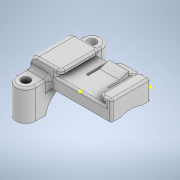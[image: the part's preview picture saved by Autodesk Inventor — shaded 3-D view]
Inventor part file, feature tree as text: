
AUTODESK INVENTOR PART (.ipt)
format: ipt  version: 2020 (Build 240168000, 168)  size: 480,256 bytes
history: native  units: mm
features: fillet x15, sketch x10, extrude x8, projected_geometry x1
ambient origin geometry x8: Origin, YZ Plane, XZ Plane, XY Plane, X Axis, Y Axis, Z Axis, Center Point
bodies: Volumenkörper1 (feature_tree)
feature tree (34):
  extrude  "Extrusion1"  Depth=24.0mm
  extrude  "Extrusion2"  Depth=2.0mm
  extrude  "Extrusion3"  Depth=2.0mm
  fillet  "Rundung1"  Radius=20.0mm
  fillet  "Rundung3"  Radius=44.0mm
  fillet  "Rundung4"  Radius=15.8mm
  fillet  "Rundung5"  Radius=22.2mm
  fillet  "Rundung6"  Radius=18.0mm
  extrude  "Extrusion4"  Depth=15.8mm
  extrude  "Extrusion5"  Depth=10.0mm
  sketch  "Skizze6"  dims[d19=4.5mm d20=5.0mm d21=5.0mm d22=5.0mm d23=5.0mm d24=0.0mm d25=0.0mm]
  extrude  "Extrusion6"  Depth=5.0mm
  fillet  "Rundung10"  Radius=5.0mm
  fillet  "Rundung11"  Radius=5.0mm
  fillet  "Rundung12"  Radius=5.0mm
  fillet  "Rundung13"  [1 undecoded]
  extrude  "Extrusion9"  Depth=10.0mm
  fillet  "Rundung15"  Radius=4.0mm
  fillet  "Rundung16"  Radius=1.0mm
  fillet  "Rundung18"  Radius=2.0mm
  fillet  "Rundung19"  Radius=1.0mm
  fillet  "Rundung20"  Radius=10.0mm
  fillet  "Rundung21"  Radius=1.0mm
  sketch  "Skizze12"  dims[d37=11.0mm]
  extrude  "Extrusion10"  Depth=13.129033mm
  sketch  "Skizze1"  dims[d0=20.0mm d2=24.0mm]
  sketch  "Skizze2"  dims[d3=32.0mm d4=2.0mm]
  sketch  "Skizze3"  dims[d5=2.0mm d6=2.0mm d7=20.0mm d8=0.0mm d9=44.0mm d10=15.8mm d11=22.2mm d12=18.0mm]
  sketch  "Skizze4"  dims[d14=22.0mm d15=15.8mm]
  sketch  "Skizze5"  dims[d16=10.0mm d17=0.0mm d18=4.5mm]
  sketch  "Skizze7"  dims[d26=18.0mm d27=5.0mm d29=4.0mm d30=1.0mm d31=2.0mm d32=1.0mm d33=10.0mm d34=1.0mm]
  sketch  "Skizze11"  dims[d35=1.0mm d36=13.129033mm]
  projected_geometry  "Projizierte Kontur1"
  sketch  "Skizze13"  dims[d38=5.0mm d39=10.0mm d40=0.0mm d41=1.5mm d42=5.0mm d43=2.0mm d44=4.363323mm d45=7.0mm d46=10.0mm d47=0.0mm d48=1.5mm d49=0.0mm d65=1.0mm d66=1.0mm d67=2.0mm d68=0.5mm d73=10.0mm d74=0.0mm d75=10.0mm d76=20.0mm d77=6.0mm d78=1.0mm d79=1.0mm d81=1.0mm d82=0.9mm d83=2.0mm d84=0.1mm d85=0.19mm d87=30.2mm d88=32.0mm d89=0.0mm d86=0.872665mm]
note: 1 required parameter value undecoded (feature->parameter linkage not recoverable at this tier; creation-order binding heuristic only, values carry confidence <= 0.55)
